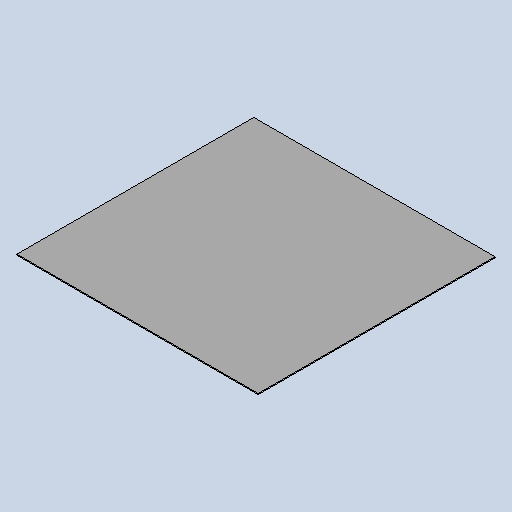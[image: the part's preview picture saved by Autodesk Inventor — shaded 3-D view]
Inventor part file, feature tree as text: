
AUTODESK INVENTOR PART (.ipt)
format: ipt  version: 2025.3 (Build 293356030, 356C)  size: 139,776 bytes
history: native  units: mm
features: other x2, sheet_metal_op x1, sketch x1
ambient origin geometry x8: Origin, YZ Plane, XZ Plane, XY Plane, X Axis, Y Axis, Z Axis, Center Point
bodies: Solid1 (feature_tree)
feature tree (4):
  sheet_metal_op  "Face1"
  sketch  "Sketch1"  dims[d2=489.0mm d3=2.0mm d18=480.0mm]
  other  "Plate1"
  other  "Definition1"
